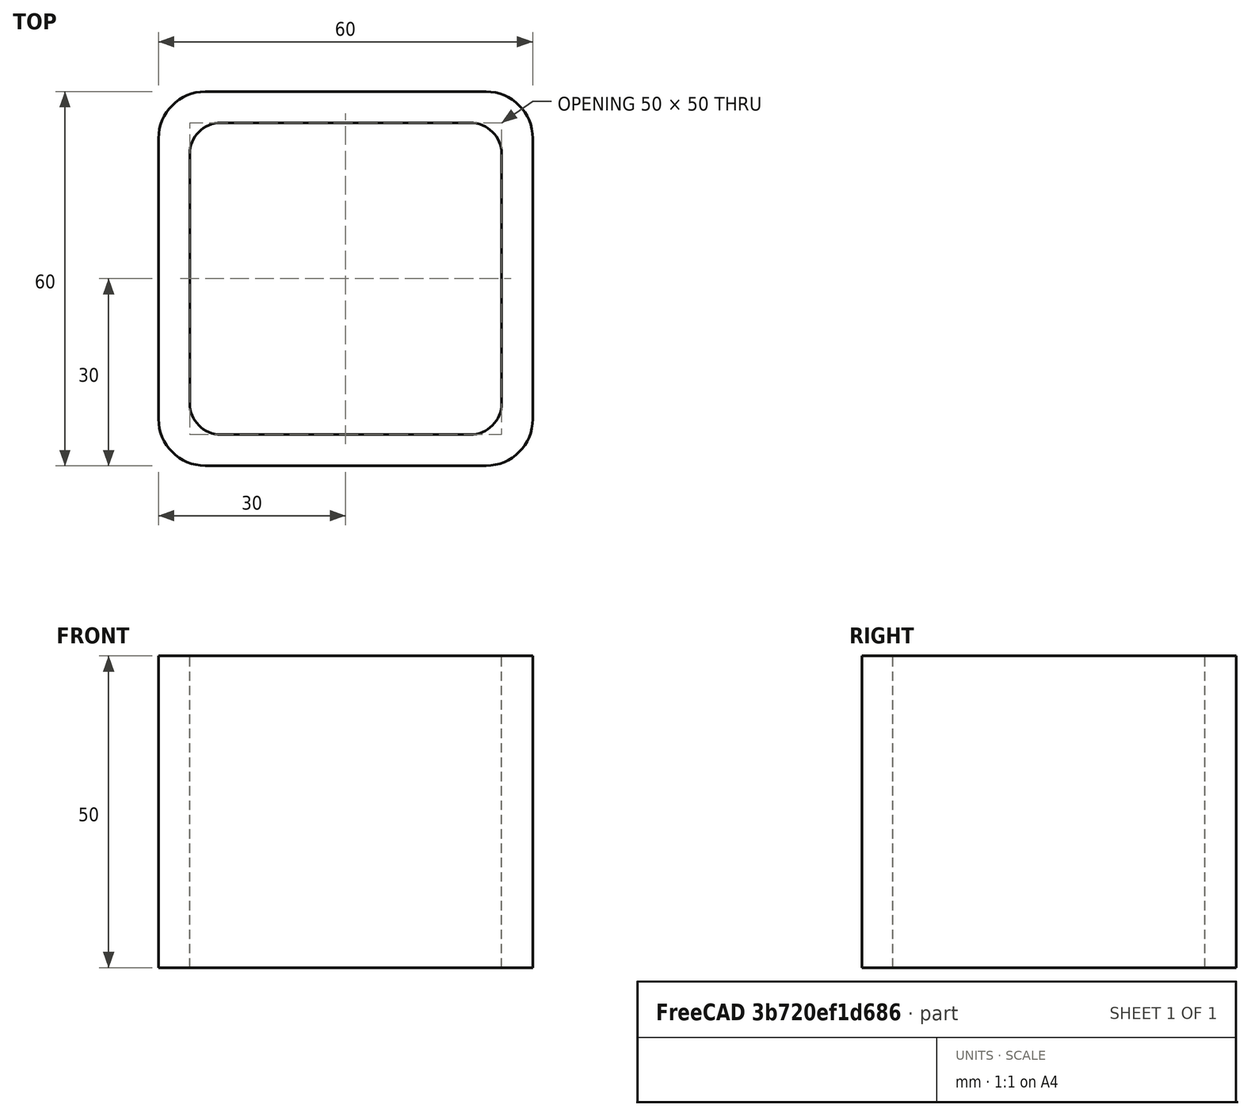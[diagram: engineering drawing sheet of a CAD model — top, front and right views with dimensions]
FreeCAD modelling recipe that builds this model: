
FCSTD DOCUMENT  (FreeCAD 0.15R4671 (Git))
Label: Square hollow section 60x60x5 EN10219 S235JRH
License: All rights reserved
LicenseURL: http://en.wikipedia.org/wiki/All_rights_reserved
objects: Sketcher::SketchObject×1, Part::Extrusion×1
note: 2 computed .brp shape members not serialized (recipe doc carries the construction recipe); baked Part::Feature solids carry a one-line shape summary decoded from their .brp

FEATURE [Sketcher::SketchObject] Sketch
  sketch-geometry (16):
    g0: LineSegment StartX=-20 StartY=25 StartZ=0 EndX=20 EndY=25 EndZ=0
    g1: LineSegment StartX=25 StartY=20 StartZ=0 EndX=25 EndY=-20 EndZ=0
    g2: LineSegment StartX=20 StartY=-25 StartZ=0 EndX=-20 EndY=-25 EndZ=0
    g3: LineSegment StartX=-25 StartY=-20 StartZ=0 EndX=-25 EndY=20 EndZ=0
    g4: LineSegment StartX=-22.5 StartY=30 StartZ=0 EndX=22.5 EndY=30 EndZ=0
    g5: LineSegment StartX=30 StartY=22.5 StartZ=0 EndX=30 EndY=-22.5 EndZ=0
    g6: LineSegment StartX=22.5 StartY=-30 StartZ=0 EndX=-22.5 EndY=-30 EndZ=0
    g7: LineSegment StartX=-30 StartY=-22.5 StartZ=0 EndX=-30 EndY=22.5 EndZ=0
    g8: ArcOfCircle CenterX=-20 CenterY=20 CenterZ=0 NormalX=0 NormalY=0 NormalZ=1 Radius=5 StartAngle=1.5708 EndAngle=3.14159
    g9: ArcOfCircle CenterX=20 CenterY=20 CenterZ=0 NormalX=0 NormalY=0 NormalZ=1 Radius=5 StartAngle=0 EndAngle=1.5708
    g10: ArcOfCircle CenterX=20 CenterY=-20 CenterZ=0 NormalX=0 NormalY=0 NormalZ=1 Radius=5 StartAngle=4.71239 EndAngle=6.28319
    g11: ArcOfCircle CenterX=-20 CenterY=-20 CenterZ=0 NormalX=0 NormalY=0 NormalZ=1 Radius=5 StartAngle=3.14159 EndAngle=4.71239
    g12: ArcOfCircle CenterX=22.5 CenterY=22.5 CenterZ=0 NormalX=0 NormalY=0 NormalZ=1 Radius=7.5 StartAngle=0 EndAngle=1.5708
    g13: ArcOfCircle CenterX=22.5 CenterY=-22.5 CenterZ=0 NormalX=0 NormalY=0 NormalZ=1 Radius=7.5 StartAngle=4.71239 EndAngle=6.28319
    g14: ArcOfCircle CenterX=-22.5 CenterY=-22.5 CenterZ=0 NormalX=0 NormalY=0 NormalZ=1 Radius=7.5 StartAngle=3.14159 EndAngle=4.71239
    g15: ArcOfCircle CenterX=-22.5 CenterY=22.5 CenterZ=0 NormalX=0 NormalY=0 NormalZ=1 Radius=7.5 StartAngle=1.5708 EndAngle=3.14159
  constraints (36):
    c: Horizontal(g2)
    c: Vertical(g3)
    c: Horizontal(g6)
    c: Vertical(g7)
    c: Tangent(g3,g8) = 1.5708
    c: Tangent(g0,g8) = 1.5708
    c: Tangent(g0,g9) = 1.5708
    c: Tangent(g1,g9) = 1.5708
    c: Tangent(g1,g10) = 1.5708
    c: Tangent(g2,g10) = 1.5708
    c: Tangent(g2,g11) = 1.5708
    c: Tangent(g3,g11) = 1.5708
    c: Tangent(g4,g12) = 1.5708
    c: Tangent(g5,g12) = 1.5708
    c: Tangent(g5,g13) = 1.5708
    c: Tangent(g6,g13) = 1.5708
    c: Tangent(g6,g14) = 1.5708
    c: Tangent(g7,g14) = 1.5708
    c: Tangent(g7,g15) = 1.5708
    c: Tangent(g4,g15) = 1.5708
    c: Equal(g9,g8)
    c: Equal(g9,g11)
    c: Equal(g9,g10)
    c: Equal(g12,g15)
    c: Equal(g12,g14)
    c: Equal(g12,g13)
    c: Symmetric(g4,g6,g-1)
    c: Symmetric(g7,g5,g-2)
    c: DistanceY(g4,g6) = -60
    c: DistanceX(g7,g5) = 60
    c: Symmetric(g3,g1,g-2)
    c: Symmetric(g0,g2,g-1)
    c: DistanceY(g0,g4) = 5
    c: DistanceX(g5,g1) = -5
    c: Radius(g9) = 5
    c: Radius(g12) = 7.5
FEATURE [Part::Extrusion] Extrude  label="Square hollow section 60x60x5 EN10219 S235JRH"
  Base = -> Sketch
  Dir = (0,0,50)
  Solid = true
